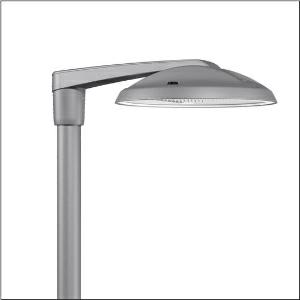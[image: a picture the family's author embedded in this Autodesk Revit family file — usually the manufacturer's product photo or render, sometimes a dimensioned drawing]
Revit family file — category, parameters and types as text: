
# Revit family: dl_r__50_mini___st1_0a_5xa248d33s08ne_6be7
name_source: partatom
category: Lighting Fixtures
units: mm (PartAtom-declared; Revit-internal decimal feet)

## family parameters
Cut with Voids When Loaded = No
Host = Face
Light Source = No
Part Type = Normal
Room Calculation Point = No
Round Connector Dimension = Use Diameter
Shared = No

## types (1)
- --- (1 x LED, 17540 lm, 112.1 W, 3000K)
    Apparent Load = 112 VA
    CIE Flux Codes = 37 72 97 100 100
    Color Rendering = 70
    Color Temperature = 3000K
    Default Elevation = 1800 mm
    Description = DL® 50 mini, mast luminaire, primary light control with lens, of PMMA, primary optical cover: cover, of toughened safety glass, transparent, light distribution: ST1.0a, light emission: direct distribution, primary light characteristic: asymmetric, installation type: post-top, side-entry, LED, High Power LED, rated luminous flux: 17.540lm, luminous efficacy: 156lm/W, light colour: 730, colour temperature: 3000K, control: overheat protection, constant luminous flux control, time-dependent luminous flux control, flexible luminous flux parameterisation, mains connection: 230..240V, AC, 50/60Hz, connection cable pre-assembled, cable length: 10,5m, start of lifetime: 112W, end of service life: 118W, reduction: 53W, luminaire housing, of diecast aluminium, powder-coated, Siteco® metallic grey (DB 702S), inclination adjustable: 0°, 5°, 10° (post-top) | 0°, -5°, -10°, -15° (side-entry), please order mast post-top element or mast side-entry element separately, diameter: 500mm, height: 115mm, post-top: for spigot size d x l = 76 x 100mm; with reducer (optional accessory) 60 x 100mm | side-entry: for spigot size d x l = 60 x 100mm; with reducer (optional accessory) 42 x 100mm, Smart Interface above, protection rating (complete): IP66, insulation class (complete): insulation class II (safety insulation), certification: CE, ENEC, VDE, impact resistance: IK08, permissible operating ambient temperature for outdoor applications: -25..+40°C, standard-compliant lighting for roads and squares, packaging unit: 1 piece

Light Distribution: ST1.0a
    Height = 115 mm
    Lamp = 1 x LED
    Lamp Light Flux = 17540 lm
    Lamp Power = 112.1 W
    Lamp count = 1
    Length = 500 mm
    Luminous efficacy = 156 lm/W
    Manufacturer = Siteco
    ModVariant = No
    Model = 5XA248D33S08NE
    Number of Poles = 1
    OnlyDefault = Yes
    Power Factor = 1
    Product Name = DL® 50 mini | ST1.0a
    Product group = mast luminaire | pylon top
    ProductGroupID = 6100
    Protection Class = Protection class II
    Protection Degree = IP 66
    RLX_Detail_Level = 1
    RLX_Emergency_Light_Flux = 0 lm
    RLX_Emergency_Type = 0
    RLX_Emergency_Type_DB = No
    RlxData = <blob elided: 106141 chars, md5=a15faeeb>
    Socket = socket
    Standby Power = 0 W
    System Light Flux = 17540 lm
    System Power = 112 W
    Type Comments = factory setting: luminous flux: 100 % | dim-lin: 254 | 601 mA
    Type Image = l_1251788.jpg
    URL = http://relux.com
    VarID = @adj_023509
    Voltage = 0 V
    Weight = 0.00 kg
    Width = 0 mm  [stored 0 ft]

note: [stored X ft] marks values corroborated as IEEE doubles in the binary element streams (Revit-internal decimal feet)

## geometry (parser evidence)
native form markers: Blend x4, Sweep x8
no freeform markers — native parametric forms only
